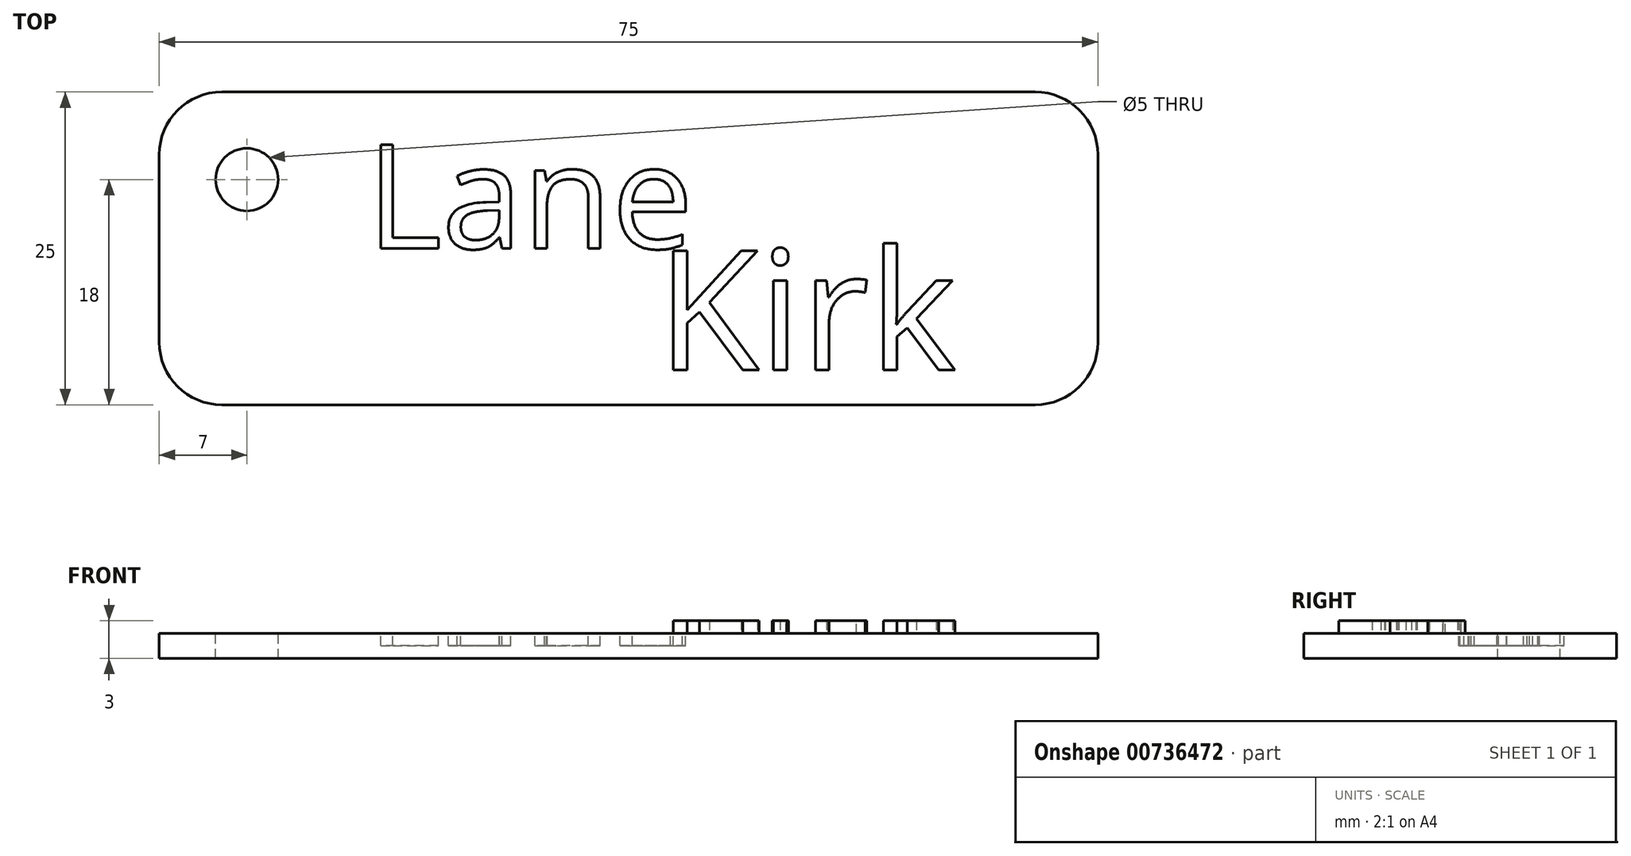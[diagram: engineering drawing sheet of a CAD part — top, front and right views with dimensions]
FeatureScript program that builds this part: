
annotation { "Feature Type Name" : "Feature", "Feature Type Description" : "" }
export const myFeature = defineFeature(function(context is Context, id is Id, definition is map)
    precondition{}
    {
        {
            var Q0;
            Q0=qCreatedBy(makeId("Top.planeOp"),FACE);
            var sketch = newSketch(context, id + "F0", { "sketchPlane" : qUnion([Q0])});
            skLineSegment(sketch, "E0.bottom", {"start": v(32.5, 12.5) * mm, "end": v(-32.5, 12.5) * mm});
            skLineSegment(sketch, "E0.top", {"start": v(32.5, -12.5) * mm, "end": v(-32.5, -12.5) * mm});
            skLineSegment(sketch, "E0.left", {"start": v(37.5, 7.5) * mm, "end": v(37.5, -7.5) * mm});
            skLineSegment(sketch, "E0.right", {"start": v(-37.5, 7.5) * mm, "end": v(-37.5, -7.5) * mm});
            skPoint(sketch, "E0.middle", {"position": v(0, 0) * mm});
            skPoint(sketch, "E1.visualSharp", {"position": v(-37.5, 12.5) * mm});
            skArc(sketch, "E1.filletArc", {"start": v(-32.5, 12.5) * mm, "mid": v(-36.04, 11.04) * mm, "end": v(-37.5, 7.5) * mm});
            skPoint(sketch, "E2.visualSharp", {"position": v(-37.5, -12.5) * mm});
            skArc(sketch, "E2.filletArc", {"start": v(-37.5, -7.5) * mm, "mid": v(-36.04, -11.04) * mm, "end": v(-32.5, -12.5) * mm});
            skPoint(sketch, "E3.visualSharp", {"position": v(37.5, -12.5) * mm});
            skArc(sketch, "E3.filletArc", {"start": v(32.5, -12.5) * mm, "mid": v(36.04, -11.04) * mm, "end": v(37.5, -7.5) * mm});
            skPoint(sketch, "E4.visualSharp", {"position": v(37.5, 12.5) * mm});
            skArc(sketch, "E4.filletArc", {"start": v(37.5, 7.5) * mm, "mid": v(36.04, 11.04) * mm, "end": v(32.5, 12.5) * mm});
            skSolve(sketch);
        }
        {
            var Q0;
            Q0=makeQuery(id+"F0.imprint","IMPRINT",FACE,{"disambiguationData":[TD([[makeQuery(id+"F0.imprint","IMPRINT",EDGE,{"derivedFrom":sQuery(id+"F0.wireOp",EDGE,"E0.bottom")}),1.0]])]});
            extrude(context, id + "F1", {"entities" : qUnion([Q0]), "depth" : 2 * mm, "offsetDistance" : 25 * mm});
        }
        {
            var Q0;
            Q0=makeQuery(id+"F1.opExtrude","CAP_FACE",FACE,{"disambiguationData":[OSD([sQuery(id+"F0.wireOp",EDGE,"E0.bottom"),sQuery(id+"F0.wireOp",EDGE,"E0.top"),sQuery(id+"F0.wireOp",EDGE,"E0.left"),sQuery(id+"F0.wireOp",EDGE,"E0.right"),sQuery(id+"F0.wireOp",EDGE,"E1.filletArc"),sQuery(id+"F0.wireOp",EDGE,"E2.filletArc"),sQuery(id+"F0.wireOp",EDGE,"E3.filletArc"),sQuery(id+"F0.wireOp",EDGE,"E4.filletArc")])],"isStart":false});
            var sketch = newSketch(context, id + "F2", { "sketchPlane" : qUnion([Q0])});
            skPoint(sketch, "E5", {"position": v(-30.5, 5.5) * mm});
            skSolve(sketch);
        }
        {
            var Q0;
            Q0=sQuery(id+"F2.wireOp",VERTEX,"E5");
            var Q1;
            Q1=makeQuery(id+"F1.opExtrude","SWEPT_BODY",BODY,{"disambiguationData":[OSD([sQuery(id+"F0.wireOp",EDGE,"E0.bottom"),sQuery(id+"F0.wireOp",EDGE,"E0.top"),sQuery(id+"F0.wireOp",EDGE,"E0.left"),sQuery(id+"F0.wireOp",EDGE,"E0.right"),sQuery(id+"F0.wireOp",EDGE,"E1.filletArc"),sQuery(id+"F0.wireOp",EDGE,"E2.filletArc"),sQuery(id+"F0.wireOp",EDGE,"E3.filletArc"),sQuery(id+"F0.wireOp",EDGE,"E4.filletArc")])]});
            hole(context, id + "F3", {"style" : HoleStyle.SIMPLE, "endStyle" : HoleEndStyle.THROUGH, "holeDiameter" : 5 * mm, "majorDiameter" : 5 * mm, "isTappedThrough" : true, "tappedDepth" : 12 * mm, "tapClearance" : 3, "locations" : qUnion([Q0]), "scope" : qUnion([Q1])});
        }
        {
            var Q0;
            Q0=makeQuery(id+"F1.opExtrude","CAP_FACE",FACE,{"disambiguationData":[OSD([sQuery(id+"F0.wireOp",EDGE,"E0.bottom"),sQuery(id+"F0.wireOp",EDGE,"E0.top"),sQuery(id+"F0.wireOp",EDGE,"E0.left"),sQuery(id+"F0.wireOp",EDGE,"E0.right"),sQuery(id+"F0.wireOp",EDGE,"E1.filletArc"),sQuery(id+"F0.wireOp",EDGE,"E2.filletArc"),sQuery(id+"F0.wireOp",EDGE,"E3.filletArc"),sQuery(id+"F0.wireOp",EDGE,"E4.filletArc")])],"isStart":false});
            var sketch = newSketch(context, id + "F4", { "sketchPlane" : qUnion([Q0])});
            skText(sketch, "E6", { "text": "Lane", "fontName": "OpenSans-Regular.ttf"});
            const initialGuessF4  = {"E6": [-0.02095, 0, 1, 0, 0.00836]};
            skSetInitialGuess(sketch, initialGuessF4);
            skSolve(sketch);
        }
        {
            var Q0;
            Q0 = qSketchRegion(id + "F4", true);
            extrude(context, id + "F5", {"entities" : qUnion([Q0]), "operationType" : NewBodyOperationType.REMOVE, "oppositeDirection" : true, "depth" : 1 * mm, "offsetDistance" : 25 * mm});
        }
        {
            var Q0;
            {var subQ0=sQuery(id+"F0.wireOp",EDGE,"E4.filletArc");var subQ1=sQuery(id+"F0.wireOp",EDGE,"E3.filletArc");var subQ2=sQuery(id+"F0.wireOp",EDGE,"E2.filletArc");var subQ3=sQuery(id+"F0.wireOp",EDGE,"E1.filletArc");var subQ4=sQuery(id+"F0.wireOp",EDGE,"E0.right");var subQ5=sQuery(id+"F0.wireOp",EDGE,"E0.top");var subQ6=sQuery(id+"F0.wireOp",EDGE,"E0.left");var subQ7=sQuery(id+"F0.wireOp",EDGE,"E0.bottom");Q0=makeQuery(id+"F5.boolean.opBoolean","SPLIT",FACE,{"disambiguationData":[TD([makeQuery(id+"F1.opExtrude","SWEPT_FACE",FACE,{"disambiguationData":[OSD([subQ7])]})])],"derivedFrom":makeQuery(id+"F1.opExtrude","CAP_FACE",FACE,{"disambiguationData":[OSD([subQ7,subQ5,subQ6,subQ4,subQ3,subQ2,subQ1,subQ0])],"isStart":false})});}
            var sketch = newSketch(context, id + "F6", { "sketchPlane" : qUnion([Q0])});
            skText(sketch, "E7", { "text": "Kirk", "fontName": "OpenSans-Regular.ttf"});
            const initialGuessF6  = {"E7": [0.00227, -0.0097, 1, 0, 0.00958]};
            skSetInitialGuess(sketch, initialGuessF6);
            skSolve(sketch);
        }
        {
            var Q0;
            Q0 = qSketchRegion(id + "F6", true);
            extrude(context, id + "F7", {"entities" : qUnion([Q0]), "operationType" : NewBodyOperationType.ADD, "depth" : 1 * mm, "offsetDistance" : 25 * mm});
        }
    });
